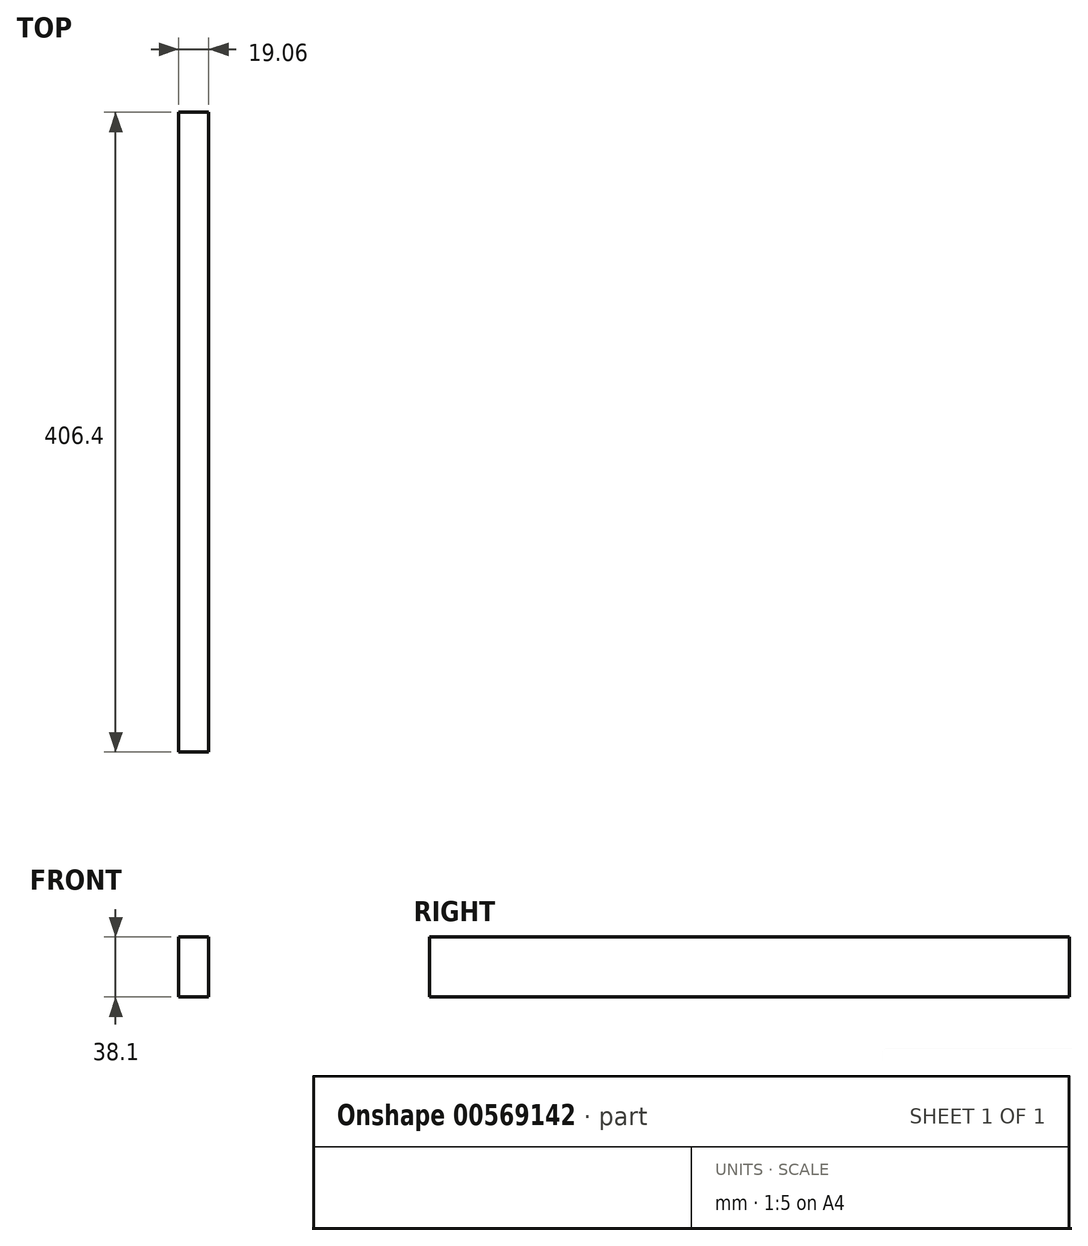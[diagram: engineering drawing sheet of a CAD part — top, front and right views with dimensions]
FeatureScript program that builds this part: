
annotation { "Feature Type Name" : "Feature", "Feature Type Description" : "" }
export const myFeature = defineFeature(function(context is Context, id is Id, definition is map)
    precondition{}
    {
        {
            var Q0;
            Q0=qCreatedBy(makeId("Right.planeOp"),FACE);
            var sketch = newSketch(context, id + "F0", { "sketchPlane" : qUnion([Q0])});
            skLineSegment(sketch, "E0.bottom", {"start": v(-203.2, 19.05) * mm, "end": v(203.2, 19.05) * mm});
            skLineSegment(sketch, "E0.top", {"start": v(-203.2, -19.05) * mm, "end": v(203.2, -19.05) * mm});
            skLineSegment(sketch, "E0.left", {"start": v(-203.2, 19.05) * mm, "end": v(-203.2, -19.05) * mm});
            skLineSegment(sketch, "E0.right", {"start": v(203.2, 19.05) * mm, "end": v(203.2, -19.05) * mm});
            skPoint(sketch, "E0.middle", {"position": v(0, 0) * mm});
            skSolve(sketch);
        }
        {
            var Q0;
            Q0=makeQuery(id+"F0.imprint","IMPRINT",FACE,{"disambiguationData":[TD([[makeQuery(id+"F0.imprint","IMPRINT",EDGE,{"derivedFrom":sQuery(id+"F0.wireOp",EDGE,"E0.bottom")}),-1.0]])]});
            extrude(context, id + "F1", {"entities" : qUnion([Q0]), "endBound" : BoundingType.SYMMETRIC, "depth" : 19.05 * mm, "offsetDistance" : 25.4 * mm});
        }
    });
